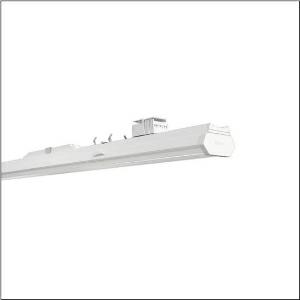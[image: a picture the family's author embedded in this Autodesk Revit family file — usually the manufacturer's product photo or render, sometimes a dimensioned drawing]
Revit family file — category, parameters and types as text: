
# Revit family: licross_11_protected_mo_51tp12dn595g
name_source: partatom
category: Lighting Fixtures
units: mm (PartAtom-declared; Revit-internal decimal feet)

## family parameters
Cut with Voids When Loaded = No
Host = Face
Light Source = No
Part Type = Normal
Room Calculation Point = No
Round Connector Dimension = Use Diameter
Shared = No

## types (1)
- --- (1 x LED, 9820 lm, 57.1 W, 5000K)
    Apparent Load = 57 VA
    CIE Flux Codes = 73 92 98 99 100
    Color Rendering = 80
    Color Temperature = 5000K
    Default Elevation = 1800 mm
    Description = Licross 11 Protected MO, luminaire insert, of sheet steel, galvanised, coil coated, white, length: 1.500mm, width: 90mm, height: 101mm, LED rated luminous flux: 9.820lm, light colour: 850, SDCM (Standard Deviation of Colour Matching)MacAdam ≤ 2 SDCM (initial), control gear: DALI 2, with plug, 5-pole, with phase selection, mains connection: 220..240V, AC, 50/60Hz, rated input power: 57W, internal wiring halogen-free, primary optical cover: cover, of PMMA, light emission: direct distribution, primary light characteristic: symmetric, protection rating (complete): IP64, insulation class (complete): insulation class I (protective earthing), certification: CE, ENEC, VDE, UKCA, protection symbol: D if used in an environment with conductive dust loads with corresponding accessories, impact resistance: IK06, permissible ambient temperature for indoor applications: -25..+35°C, corresponds to IFS (International Featured Standards) requirements for safety and quality in the food industry, reducing of maximum allowable ambient temperature of 5°C with ceiling mounting, LABS conformity tested according to VDMA 24364:2018-05, The light source and the operating device comply with the requirements of the Ecodesign Regulation (EU) 2019/2020 and are replaceable in accordance with this regulation, packaging unit: 1 piece
    Height = 92 mm
    Lamp = 1 x LED
    Lamp Light Flux = 9820 lm
    Lamp Power = 57.1 W
    Lamp count = 1
    Length = 1500 mm
    Luminous efficacy = 172 lm/W
    Manufacturer = Siteco
    ModVariant = No
    Model = 51TP12DN595G
    Mounting Place = Ceiling
    Mounting Type = Pendant
    Number of Poles = 1
    OnlyDefault = Yes
    Power Factor = 1
    Product Name = Licross 11 Protected MO
    Product group = luminaire insert | ceiling pendant
    ProductGroupID = 901
    Protection Class = Protection class I
    Protection Degree = IP 64
    RLX_Detail_Level = 1
    RLX_Emergency_Light_Flux = 0 lm
    RLX_Emergency_Type = 0
    RLX_Emergency_Type_DB = No
    RlxData = <blob elided: 24721 chars, md5=3f13e3d2>
    Socket = socket
    Standby Power = 0 W
    System Light Flux = 9820 lm
    System Power = 57 W
    Type Comments = factory setting: luminous flux: 100 % | dim-lin: 254 | 378 mA
    Type Image = l_1256148.jpg
    URL = http://relux.com
    VarID = @adj_037475
    Voltage = 0 V
    Weight = 0.00 kg
    Width = 88 mm

## geometry (parser evidence)
native form markers: Blend x4, Sweep x10
no freeform markers — native parametric forms only
